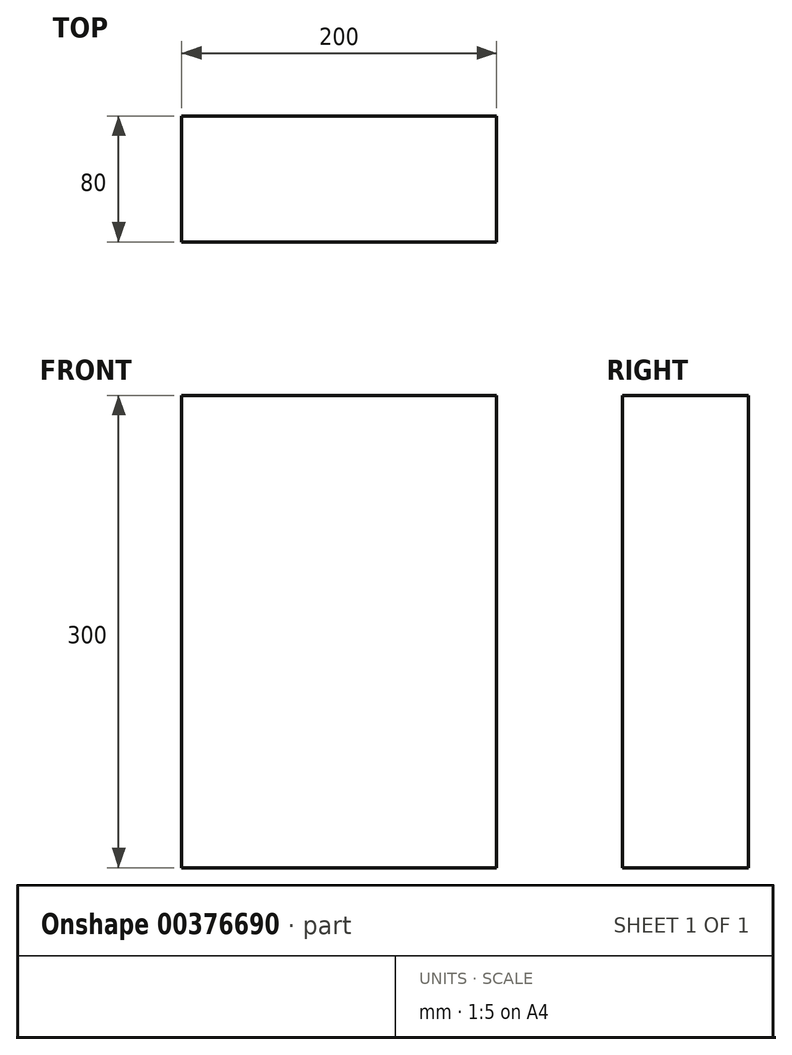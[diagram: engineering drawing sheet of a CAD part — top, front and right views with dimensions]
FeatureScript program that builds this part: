
annotation { "Feature Type Name" : "Feature", "Feature Type Description" : "" }
export const myFeature = defineFeature(function(context is Context, id is Id, definition is map)
    precondition{}
    {
        {
            var Q0;
            Q0=qCreatedBy(makeId("Top.planeOp"),FACE);
            var sketch = newSketch(context, id + "F0", { "sketchPlane" : qUnion([Q0])});
            skLineSegment(sketch, "E0.bottom", {"start": v(-100, -40) * mm, "end": v(100, -40) * mm});
            skLineSegment(sketch, "E0.top", {"start": v(-100, 40) * mm, "end": v(100, 40) * mm});
            skLineSegment(sketch, "E0.left", {"start": v(-100, -40) * mm, "end": v(-100, 40) * mm});
            skLineSegment(sketch, "E0.right", {"start": v(100, -40) * mm, "end": v(100, 40) * mm});
            skPoint(sketch, "E0.middle", {"position": v(0, 0) * mm});
            skSolve(sketch);
        }
        {
            var Q0;
            Q0 = qSketchRegion(id + "F0", true);
            extrude(context, id + "F1", {"entities" : qUnion([Q0]), "endBound" : BoundingType.SYMMETRIC, "depth" : 300 * mm});
        }
    });
